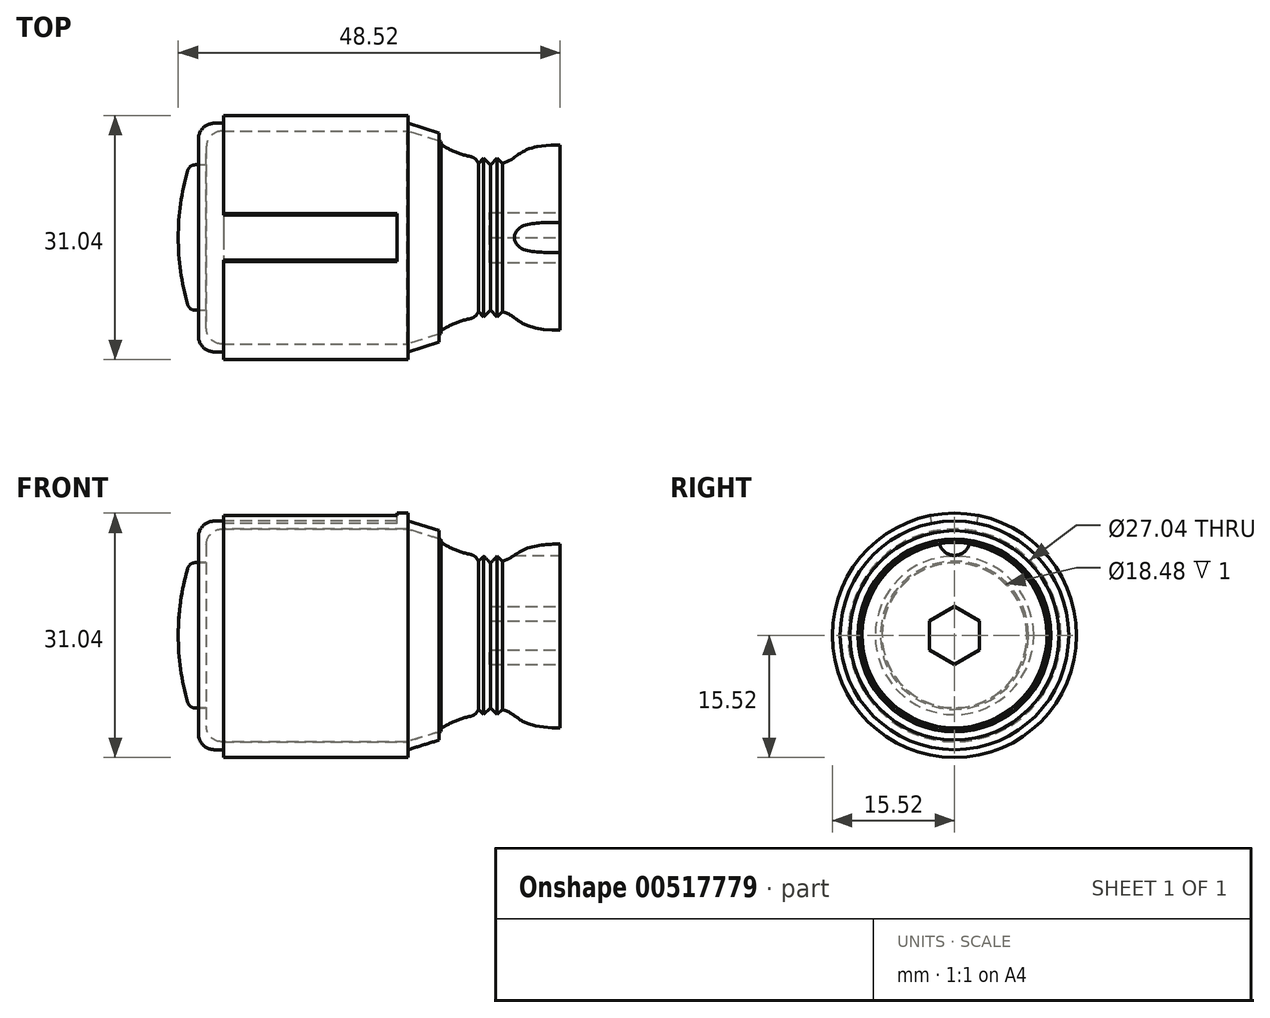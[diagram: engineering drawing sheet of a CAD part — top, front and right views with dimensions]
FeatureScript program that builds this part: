
annotation { "Feature Type Name" : "Feature", "Feature Type Description" : "" }
export const myFeature = defineFeature(function(context is Context, id is Id, definition is map)
    precondition{}
    {
        {
            var Q0;
            Q0=qCreatedBy(makeId("Front.planeOp"),FACE);
            var sketch = newSketch(context, id + "F0", { "sketchPlane" : qUnion([Q0])});
            skLineSegment(sketch, "E0", {"start": v(0, 41.31) * mm, "end": v(0, -41.31) * mm, "construction": true});
            skLineSegment(sketch, "E1", {"start": v(-41.31, 0) * mm, "end": v(0, 0) * mm, "construction": true});
            skLineSegment(sketch, "E2", {"start": v(0, 0) * mm, "end": v(41.31, 0) * mm, "construction": true});
            skSolve(sketch);
        }
        {
            var Q0;
            Q0=qCreatedBy(makeId("Front.planeOp"),FACE);
            var sketch = newSketch(context, id + "F1", { "sketchPlane" : qUnion([Q0])});
            skLineSegment(sketch, "E3", {"start": v(47.86, 0) * mm, "end": v(-47.86, 0) * mm, "construction": true});
            skLineSegment(sketch, "E4", {"start": v(-8.87, 0) * mm, "end": v(-8.87, 11.76) * mm});
            skLineSegment(sketch, "E5", {"start": v(-1.53, 9.41) * mm, "end": v(-0.85, 10.07) * mm});
            skLineSegment(sketch, "E6", {"start": v(-0.85, 10.07) * mm, "end": v(0, 9.19) * mm});
            skLineSegment(sketch, "E7.MirrorCS", {"start": v(0.85, 10.07) * mm, "end": v(0, 9.19) * mm});
            skLineSegment(sketch, "E8.MirrorCS", {"start": v(1.53, 9.41) * mm, "end": v(0.85, 10.07) * mm});
            skArc(sketch, "E9", {"start": v(2.54, 10.29) * mm, "mid": v(1.92, 9.98) * mm, "end": v(1.53, 9.41) * mm});
            skArc(sketch, "E10", {"start": v(2.54, 10.29) * mm, "mid": v(4.47, 10.87) * mm, "end": v(6.25, 11.81) * mm});
            skLineSegment(sketch, "E11", {"start": v(6.25, 11.81) * mm, "end": v(6.25, 12.17) * mm});
            skLineSegment(sketch, "E12", {"start": v(6.5, 13.3) * mm, "end": v(10.44, 14.52) * mm});
            skLineSegment(sketch, "E13", {"start": v(10.44, 15.52) * mm, "end": v(10.44, 14.52) * mm});
            skLineSegment(sketch, "E14", {"start": v(10.44, 15.52) * mm, "end": v(33.88, 15.52) * mm});
            skLineSegment(sketch, "E15", {"start": v(33.88, 15.52) * mm, "end": v(33.88, 14.52) * mm});
            skLineSegment(sketch, "E16", {"start": v(37.08, 12.52) * mm, "end": v(37.08, 9.24) * mm});
            skLineSegment(sketch, "E17", {"start": v(37.08, 9.24) * mm, "end": v(38.23, 9.24) * mm});
            skLineSegment(sketch, "E18", {"start": v(10.44, 14.52) * mm, "end": v(35.08, 14.52) * mm});
            skArc(sketch, "E19", {"start": v(39.65, 0) * mm, "mid": v(39.3, 4.67) * mm, "end": v(38.23, 9.24) * mm});
            skLineSegment(sketch, "E20.0", {"start": v(10.59, 13.52) * mm, "end": v(34.08, 13.52) * mm});
            skLineSegment(sketch, "E20.1", {"start": v(6.25, 12.17) * mm, "end": v(10.59, 13.52) * mm});
            skLineSegment(sketch, "E21", {"start": v(-8.87, 0) * mm, "end": v(39.65, 0) * mm});
            skLineSegment(sketch, "E22", {"start": v(6.5, 13.3) * mm, "end": v(6.5, 12.25) * mm});
            skLineSegment(sketch, "E23.0", {"start": v(36.08, 11.52) * mm, "end": v(36.08, 9.24) * mm});
            skLineSegment(sketch, "E24", {"start": v(36.08, 9.24) * mm, "end": v(37.08, 9.24) * mm});
            skPoint(sketch, "E25.visualSharp", {"position": v(36.08, 13.52) * mm});
            skArc(sketch, "E25.filletArc", {"start": v(36.08, 11.52) * mm, "mid": v(35.5, 12.93) * mm, "end": v(34.08, 13.52) * mm});
            skPoint(sketch, "E26.visualSharp", {"position": v(37.08, 14.52) * mm});
            skArc(sketch, "E26.filletArc", {"start": v(37.08, 12.52) * mm, "mid": v(36.5, 13.93) * mm, "end": v(35.08, 14.52) * mm});
            skFitSpline(sketch, "E27", {"points": [v(-1.53, 9.41) * mm, v(-8.87, 11.76) * mm], "startDerivative": vector(-7.34, 2.31) * mm, "endDerivative": vector(-16.55, 0) * mm});
            skSolve(sketch);
        }
        {
            var Q0;
            Q0=makeQuery(id+"F1.imprint","IMPRINT",FACE,{"disambiguationData":[TD([[makeQuery(id+"F1.imprint","IMPRINT",EDGE,{"derivedFrom":sQuery(id+"F1.wireOp",EDGE,"E4")}),-1.0]])]});
            var Q1;
            Q1=sQuery(id+"F1.wireOp",EDGE,"E21");
            revolve(context, id + "F2", {"entities" : qUnion([Q0]), "axis" : qUnion([Q1]), "revolveType" : RevolveType.FULL});
        }
        {
            var Q0;
            {var subQ3=sQuery(id+"F1.wireOp",EDGE,"E12");Q0=makeQuery(id+"F1.imprint","IMPRINT",FACE,{"disambiguationData":[TD([[makeQuery(id+"F1.imprint","IMPRINT",EDGE,{"derivedFrom":subQ3}),-1.0]])]});}
            var Q1;
            {var subQ0=sQuery(id+"F1.wireOp",EDGE,"E13");Q1=makeQuery(id+"F1.imprint","IMPRINT",FACE,{"disambiguationData":[TD([[makeQuery(id+"F1.imprint","IMPRINT",EDGE,{"derivedFrom":subQ0}),1.0]])]});}
            var Q2;
            Q2=sQuery(id+"F1.wireOp",EDGE,"E3");
            revolve(context, id + "F3", {"entities" : qUnion([Q0, Q1]), "axis" : qUnion([Q2]), "revolveType" : RevolveType.FULL});
        }
        {
            var Q0;
            Q0=makeQuery(id+"F3.opRevolve","SWEPT_FACE",FACE,{"disambiguationData":[OSD([sQuery(id+"F1.wireOp",EDGE,"E15")])]});
            var sketch = newSketch(context, id + "F4", { "sketchPlane" : qUnion([Q0])});
            skLineSegment(sketch, "E28", {"start": v(-19.95, 0) * mm, "end": v(0, 0) * mm, "construction": true});
            skCircle(sketch, "E29.0", {"center": v(0, 0) * mm, "radius": 15.52 * mm, "construction": true});
            skCircle(sketch, "E30.0", {"center": v(0, 0) * mm, "radius": 14.52 * mm, "construction": true});
            skLineSegment(sketch, "E31", {"start": v(-3, 15.02) * mm, "end": v(3, 15.02) * mm, "construction": true});
            skPoint(sketch, "E32", {"position": v(0, 14.52) * mm});
            skLineSegment(sketch, "E33", {"start": v(0, 15.52) * mm, "end": v(0, 14.52) * mm, "construction": true});
            skPoint(sketch, "E34", {"position": v(0, 15.02) * mm});
            skLineSegment(sketch, "E35", {"start": v(0, 0) * mm, "end": v(-3.47, 17.36) * mm});
            skLineSegment(sketch, "E36", {"start": v(0, 0) * mm, "end": v(3.47, 17.36) * mm});
            skLineSegment(sketch, "E37", {"start": v(-4.16, 17.36) * mm, "end": v(4.16, 17.36) * mm});
            skPoint(sketch, "E38", {"position": v(0, 17.36) * mm});
            skSolve(sketch);
        }
        {
            var Q0;
            {var subQ0=sQuery(id+"F4.wireOp",EDGE,"E35");var subQ1=sQuery(id+"F1.wireOp",EDGE,"E15");var subQ2=makeQuery(id+"F3.opRevolve","SWEPT_EDGE",EDGE,{"disambiguationData":[OSD([sQuery(id+"F1.wireOp",EDGE,"E14"),subQ1])]});var subQ3=makeQuery(id+"F4.imprint","INTERSECT",VERTEX,{"derivedFrom":[subQ2,subQ0]});Q0=makeQuery(id+"F4.imprint","IMPRINT",FACE,{"disambiguationData":[TD([[makeQuery(id+"F4.imprint","IMPRINT",EDGE,{"disambiguationData":[TD([[subQ3,1.0]])],"derivedFrom":subQ0}),-1.0]])]});}
            extrude(context, id + "F5", {"entities" : qUnion([Q0]), "operationType" : NewBodyOperationType.REMOVE, "oppositeDirection" : true, "depth" : 22 * mm, "offsetDistance" : 25 * mm});
        }
        {
            var Q0;
            Q0=makeQuery(id+"F2.opRevolve","SWEPT_EDGE",EDGE,{"disambiguationData":[OSD([sQuery(id+"F1.wireOp",EDGE,"E17"),sQuery(id+"F1.wireOp",EDGE,"E19")])]});
            fillet(context, id + "F6", {"entities" : qUnion([Q0]), "radius" : 1 * mm, "tangentPropagation" : true, "allowEdgeOverflow" : false});
        }
        {
            var Q0;
            Q0=makeQuery(id+"F2.opRevolve","SWEPT_FACE",FACE,{"disambiguationData":[OSD([sQuery(id+"F1.wireOp",EDGE,"E4")])]});
            var sketch = newSketch(context, id + "F7", { "sketchPlane" : qUnion([Q0])});
            skLineSegment(sketch, "E39", {"start": v(0, 0) * mm, "end": v(0, 19.11) * mm, "construction": true});
            skCircle(sketch, "E40", {"center": v(0, 12.18) * mm, "radius": 2 * mm});
            skSolve(sketch);
        }
        {
            var Q0;
            {var subQ0=sQuery(id+"F7.wireOp",EDGE,"E40");var subQ1=makeQuery(id+"F2.opRevolve","SWEPT_EDGE",EDGE,{"disambiguationData":[OSD([sQuery(id+"F1.wireOp",EDGE,"E4"),sQuery(id+"F1.wireOp",EDGE,"E27")])]});var subQ2=makeQuery(id+"F7.imprint","INTERSECT",VERTEX,{"disambiguationData":[OD(0.0)],"derivedFrom":[subQ1,subQ0]});Q0=makeQuery(id+"F7.imprint","IMPRINT",FACE,{"disambiguationData":[TD([[makeQuery(id+"F7.imprint","IMPRINT",EDGE,{"disambiguationData":[TD([[subQ2,1.0]])],"derivedFrom":subQ0}),1.0]])]});}
            var Q1;
            {var subQ0=sQuery(id+"F7.wireOp",EDGE,"E40");var subQ1=makeQuery(id+"F2.opRevolve","SWEPT_EDGE",EDGE,{"disambiguationData":[OSD([sQuery(id+"F1.wireOp",EDGE,"E4"),sQuery(id+"F1.wireOp",EDGE,"E27")])]});var subQ2=makeQuery(id+"F7.imprint","INTERSECT",VERTEX,{"disambiguationData":[OD(0.0)],"derivedFrom":[subQ1,subQ0]});Q1=makeQuery(id+"F7.imprint","IMPRINT",FACE,{"disambiguationData":[TD([[makeQuery(id+"F7.imprint","IMPRINT",EDGE,{"disambiguationData":[TD([[subQ2,-1.0]])],"derivedFrom":subQ0}),1.0]])]});}
            var Q2;
            Q2=makeQuery(id+"F3.opRevolve","SWEPT_BODY",BODY,{"disambiguationData":[OSD([sQuery(id+"F1.wireOp",EDGE,"E12"),sQuery(id+"F1.wireOp",EDGE,"E13"),sQuery(id+"F1.wireOp",EDGE,"E14"),sQuery(id+"F1.wireOp",EDGE,"E15"),sQuery(id+"F1.wireOp",EDGE,"E16"),sQuery(id+"F1.wireOp",EDGE,"E18"),sQuery(id+"F1.wireOp",EDGE,"E20.0"),sQuery(id+"F1.wireOp",EDGE,"E20.1"),sQuery(id+"F1.wireOp",EDGE,"E22"),sQuery(id+"F1.wireOp",EDGE,"E23.0"),sQuery(id+"F1.wireOp",EDGE,"E24"),sQuery(id+"F1.wireOp",EDGE,"E25.filletArc"),sQuery(id+"F1.wireOp",EDGE,"E26.filletArc")])]});
            extrude(context, id + "F8", {"entities" : qUnion([Q0, Q1]), "operationType" : NewBodyOperationType.REMOVE, "oppositeDirection" : true, "depth" : 6.9 * mm, "endBoundEntityBody" : qUnion([Q2]), "offsetDistance" : 25 * mm});
        }
        {
            var Q0;
            Q0=makeQuery(id+"F2.opRevolve","SWEPT_FACE",FACE,{"disambiguationData":[OSD([sQuery(id+"F1.wireOp",EDGE,"E4")])]});
            var sketch = newSketch(context, id + "F9", { "sketchPlane" : qUnion([Q0])});
            skCircle(sketch, "E41.cCircle", {"center": v(0, 0) * mm, "radius": 3.17 * mm, "construction": true});
            skLineSegment(sketch, "E41.0", {"start": v(3.18, 1.83) * mm, "end": v(3.18, -1.83) * mm});
            skLineSegment(sketch, "E41.1", {"start": v(3.18, -1.83) * mm, "end": v(0, -3.67) * mm});
            skLineSegment(sketch, "E41.2", {"start": v(0, -3.67) * mm, "end": v(-3.18, -1.83) * mm});
            skLineSegment(sketch, "E41.3", {"start": v(-3.18, -1.83) * mm, "end": v(-3.18, 1.83) * mm});
            skLineSegment(sketch, "E41.4", {"start": v(-3.18, 1.83) * mm, "end": v(0, 3.67) * mm});
            skLineSegment(sketch, "E41.5", {"start": v(0, 3.67) * mm, "end": v(3.18, 1.83) * mm});
            skPoint(sketch, "E41.0.midPoint", {"position": v(3.17, 0) * mm});
            skSolve(sketch);
        }
        {
            var Q0;
            Q0=makeQuery(id+"F9.imprint","IMPRINT",FACE,{"disambiguationData":[TD([[makeQuery(id+"F9.imprint","IMPRINT",EDGE,{"derivedFrom":sQuery(id+"F9.wireOp",EDGE,"E41.0")}),-1.0]])]});
            extrude(context, id + "F10", {"entities" : qUnion([Q0]), "operationType" : NewBodyOperationType.REMOVE, "oppositeDirection" : true, "depth" : 9 * mm, "offsetDistance" : 25 * mm});
        }
        {
            var Q0;
            Q0=qCreatedBy(makeId("Right.planeOp"),FACE);
            var sketch = newSketch(context, id + "F11", { "sketchPlane" : qUnion([Q0])});
            skLineSegment(sketch, "E42", {"start": v(0, 0) * mm, "end": v(0, 42.55) * mm, "construction": true});
            skSolve(sketch);
        }
        {
            var Q0;
            Q0=makeQuery(id+"F2.opRevolve","SWEPT_BODY",BODY,{"disambiguationData":[OSD([sQuery(id+"F1.wireOp",EDGE,"E4"),sQuery(id+"F1.wireOp",EDGE,"E5"),sQuery(id+"F1.wireOp",EDGE,"E6"),sQuery(id+"F1.wireOp",EDGE,"E7.MirrorCS"),sQuery(id+"F1.wireOp",EDGE,"E8.MirrorCS"),sQuery(id+"F1.wireOp",EDGE,"E9"),sQuery(id+"F1.wireOp",EDGE,"E10"),sQuery(id+"F1.wireOp",EDGE,"E11"),sQuery(id+"F1.wireOp",EDGE,"E17"),sQuery(id+"F1.wireOp",EDGE,"E19"),sQuery(id+"F1.wireOp",EDGE,"E20.0"),sQuery(id+"F1.wireOp",EDGE,"E20.1"),sQuery(id+"F1.wireOp",EDGE,"E21"),sQuery(id+"F1.wireOp",EDGE,"E23.0"),sQuery(id+"F1.wireOp",EDGE,"E24"),sQuery(id+"F1.wireOp",EDGE,"E25.filletArc"),sQuery(id+"F1.wireOp",EDGE,"E27")])]});
            var Q1;
            Q1=makeQuery(id+"F3.opRevolve","SWEPT_BODY",BODY,{"disambiguationData":[OSD([sQuery(id+"F1.wireOp",EDGE,"E12"),sQuery(id+"F1.wireOp",EDGE,"E13"),sQuery(id+"F1.wireOp",EDGE,"E14"),sQuery(id+"F1.wireOp",EDGE,"E15"),sQuery(id+"F1.wireOp",EDGE,"E16"),sQuery(id+"F1.wireOp",EDGE,"E18"),sQuery(id+"F1.wireOp",EDGE,"E20.0"),sQuery(id+"F1.wireOp",EDGE,"E20.1"),sQuery(id+"F1.wireOp",EDGE,"E22"),sQuery(id+"F1.wireOp",EDGE,"E23.0"),sQuery(id+"F1.wireOp",EDGE,"E24"),sQuery(id+"F1.wireOp",EDGE,"E25.filletArc"),sQuery(id+"F1.wireOp",EDGE,"E26.filletArc")])]});
            var Q2;
            Q2=sQuery(id+"F11.wireOp",EDGE,"E42");
            transform(context, id + "F12", {"entities" : qUnion([Q0, Q1]), "transformType" : TransformType.ROTATION, "transformAxis" : qUnion([Q2]), "angle" : 180 * degree, "makeCopy" : false});
        }
    });
